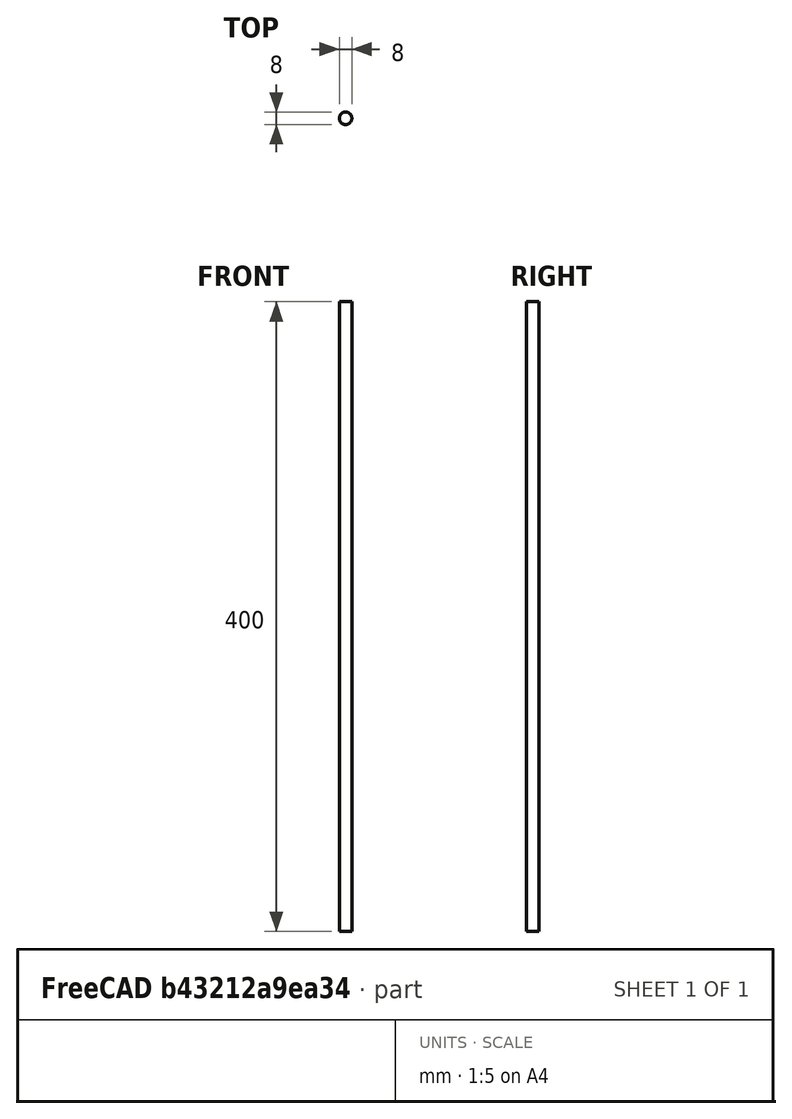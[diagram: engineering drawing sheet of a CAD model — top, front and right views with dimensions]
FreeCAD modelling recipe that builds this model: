
FCSTD DOCUMENT  (FreeCAD 0.19R)
Label: shaft_8mm
License: All rights reserved
LicenseURL: http://en.wikipedia.org/wiki/All_rights_reserved
objects: PartDesign::CoordinateSystem×2, Sketcher::SketchObject×1, PartDesign::Pad×1, PartDesign::Body×1
note: 6 computed .brp shape members not serialized (recipe doc carries the construction recipe); baked Part::Feature solids carry a one-line shape summary decoded from their .brp

FEATURE [Sketcher::SketchObject] Sketch
  FullyConstrained = true
  MapMode = 5
  Support = -> [XY_Plane]
  sketch-geometry (1):
    g0: Circle CenterX=0 CenterY=0 CenterZ=0 NormalX=0 NormalY=0 NormalZ=1 AngleXU=0 Radius=4
  constraints (2):
    c: Coincident(g0,g-1)
    c: Diameter(g0) = 8
FEATURE [PartDesign::Pad] Pad
  Direction = (1,1,1)
  Length = 400
  Length2 = 100
  Profile = -> Sketch
  Refine = true
  Type = 0
FEATURE [PartDesign::CoordinateSystem] Local_CS
  AttacherType = Attacher::AttachEngine3D
  MapMode = 11
  Placement = pos=(0,0,400) rot=(0,0,1;1.5708rad)
  Support = -> [Pad]
FEATURE [PartDesign::CoordinateSystem] Local_CS001
  AttacherType = Attacher::AttachEngine3D
  MapMode = 11
  Placement = pos=(0,0,0) rot=(0,0,1;1.5708rad)
  Support = -> [Pad]
FEATURE [PartDesign::Body] Body
  Group = -> [Sketch,Pad,Local_CS,Local_CS001]
  Origin = -> Origin
  Tip = -> Pad
